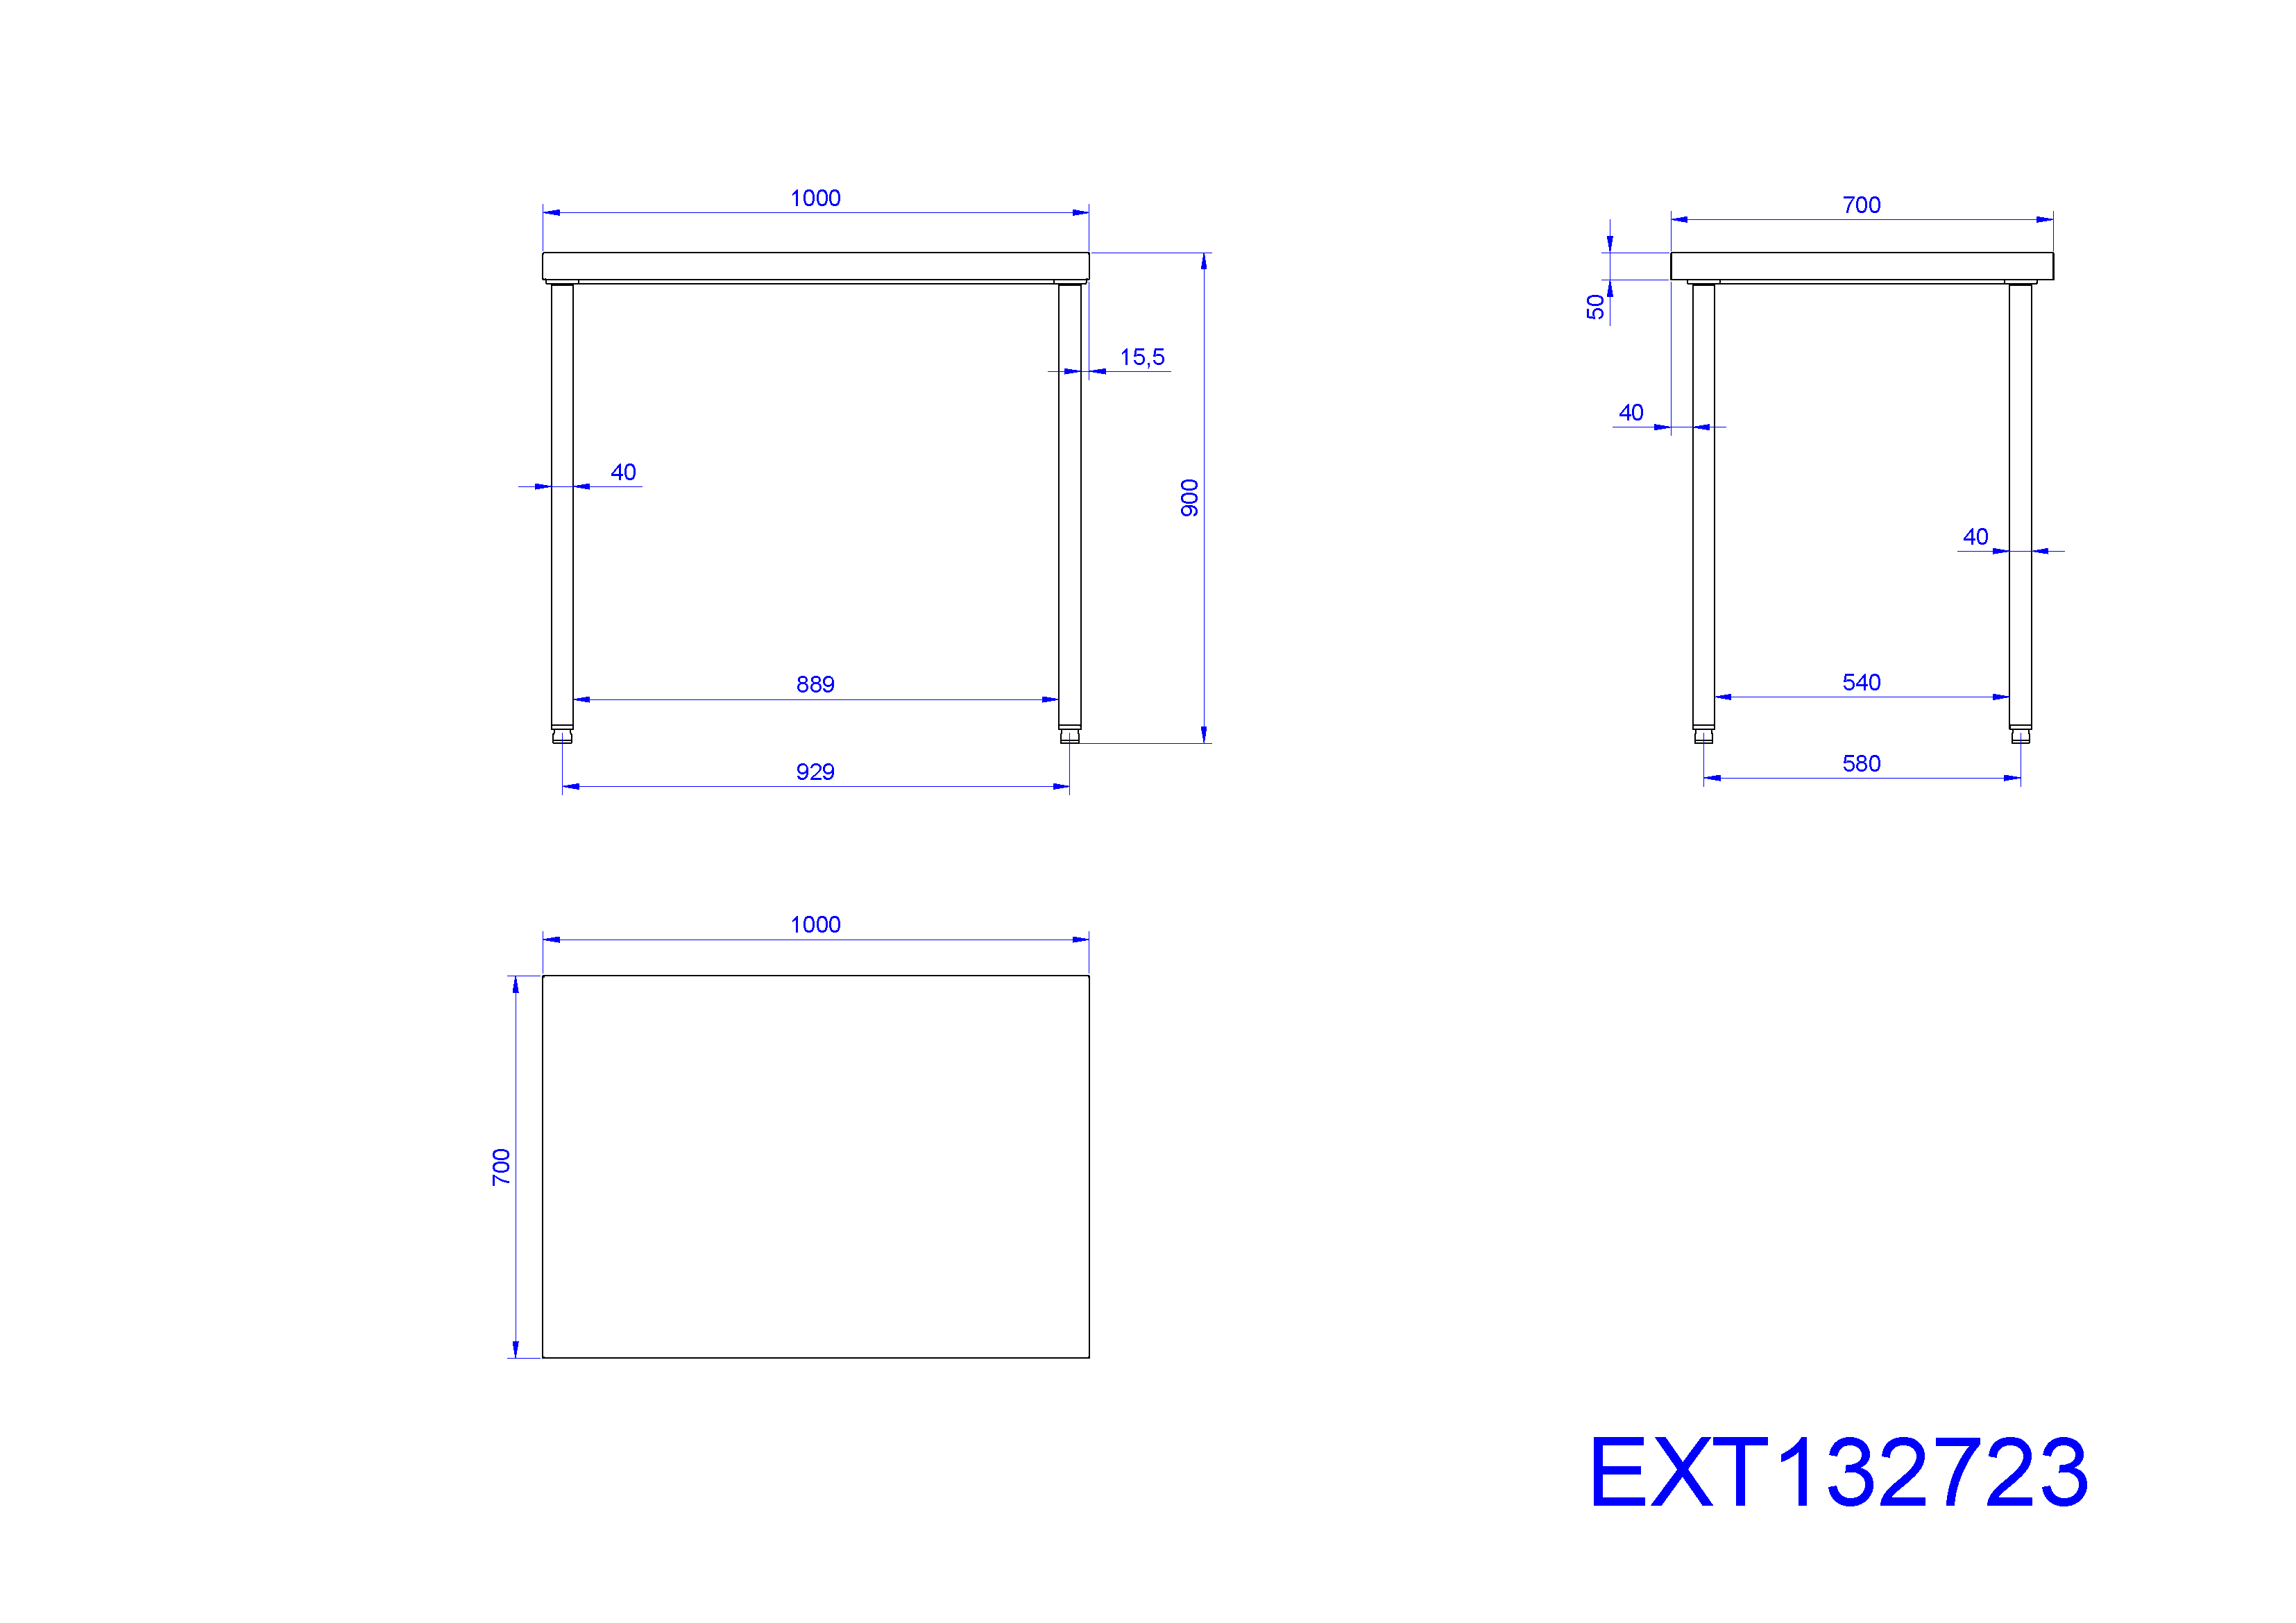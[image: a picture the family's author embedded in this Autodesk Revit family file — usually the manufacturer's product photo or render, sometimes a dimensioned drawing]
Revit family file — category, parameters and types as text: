
# Revit family: QF_ZANUSSI_132839_WTD1007N
name_source: partatom
category: Attrezzature speciali
units: mm (PartAtom-declared; Revit-internal decimal feet)

## family parameters
Basato su piano di lavoro = No
Condiviso = No
Punto di calcolo locali = No
Quota connettore circolare = Usa diametro
Sempre verticale = Sì
Taglio con vuoti quando caricato = No
Tipo di parte = Normale

## types (1)
- Standard
    Accessory = Sì
    Cold Water Size = 0 mm
    Compressed Air Pressure = 0.0 Pa
    Compressed Air Size = 0 mm
    Compressed Air Volume = 0.0 L/s
    Condensate Return Size = 0 mm
    Cycle = 0 Hz
    Depth Actual = 700 mm  [stored 2.29659 ft]
    Descrizione = WORK TABLE-DISASSEMBLED 1000MM
    Direct Waste Size = 0 mm
    Gas Input Pressure = 0
    Gas KW = 0
    Gas Size = 0 mm
    HP = 0 HP
    Height Actual = 900 mm  [stored 2.95276 ft]
    Hot Water Size = 0 mm
    Item Number = 132839
    Length Actual = 1000 mm  [stored 3.28084 ft]
    Modello = WTD1007N
    Phase = 0
    Produttore = Zanussi
    Prospetto di default = 0 mm  [stored 0 ft]
    Refrigerant Compressor Remote = Sì
    Refrigeration Liquid Line Size = 0 mm  [stored 0 ft]
    Refrigeration Suction Line Size = 0 mm  [stored 0 ft]
    Steam Consumption per Hour = 0
    Steam Supply Maximum Pressure = 0.0 Pa
    Steam Supply Minimum Pressure = 0.0 Pa
    Steam Supply Size = 0 mm
    URL = http://www.zanussiprofessional.com
    URL Manufacturer = http://www.zanussiprofessional.com
    Volts = 0 V
    Watts = 0 W
    Weight = 37.00 kg

note: source unit labels omitted for Gas Input Pressure — the stored unit's dimension contradicts the parameter name (converter mislabeling)

note: [stored X ft] marks values corroborated as IEEE doubles in the binary element streams (Revit-internal decimal feet)

## geometry (parser evidence)
native form markers: Sweep x2
no freeform markers — native parametric forms only
